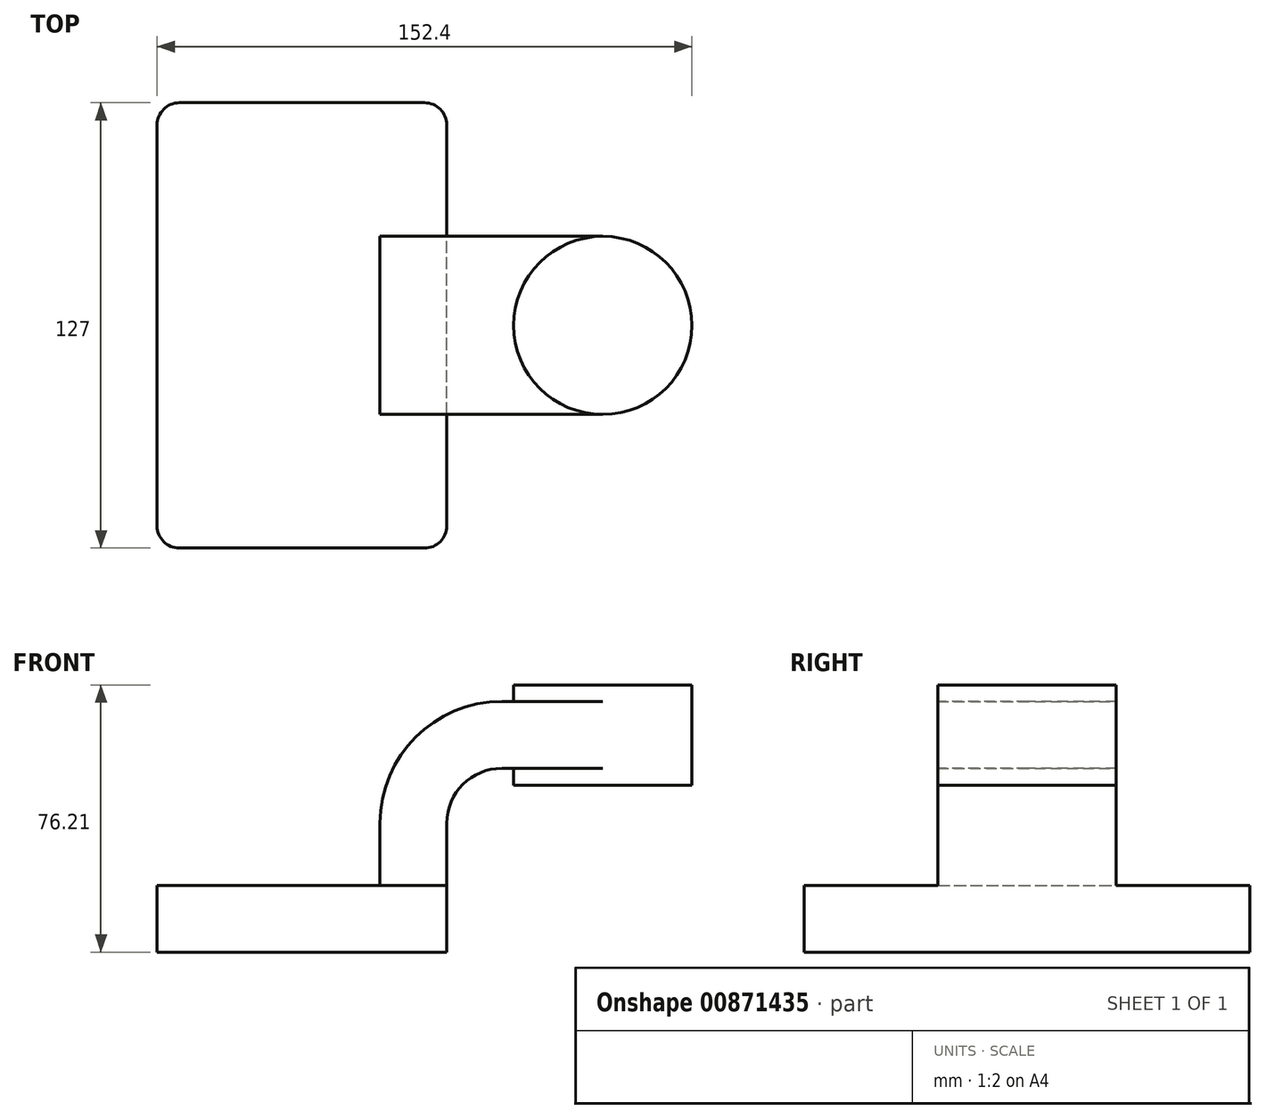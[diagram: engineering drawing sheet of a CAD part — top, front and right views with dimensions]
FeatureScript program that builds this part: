
annotation { "Feature Type Name" : "Feature", "Feature Type Description" : "" }
export const myFeature = defineFeature(function(context is Context, id is Id, definition is map)
    precondition{}
    {
        {
            var Q0;
            Q0=qCreatedBy(makeId("Front.planeOp"),FACE);
            var sketch = newSketch(context, id + "F0", { "sketchPlane" : qUnion([Q0])});
            skLineSegment(sketch, "E0.bottom", {"start": v(-41.27, -9.53) * mm, "end": v(41.28, -9.53) * mm});
            skLineSegment(sketch, "E0.top", {"start": v(-41.28, 9.53) * mm, "end": v(41.27, 9.53) * mm});
            skLineSegment(sketch, "E0.left", {"start": v(-41.27, -9.53) * mm, "end": v(-41.28, 9.53) * mm});
            skLineSegment(sketch, "E0.right", {"start": v(41.28, -9.53) * mm, "end": v(41.27, 9.53) * mm});
            skPoint(sketch, "E0.middle", {"position": v(0, 0) * mm});
            skLineSegment(sketch, "E1.bottom", {"start": v(111.12, 38.1) * mm, "end": v(60.33, 38.1) * mm});
            skLineSegment(sketch, "E1.top", {"start": v(111.13, 66.67) * mm, "end": v(60.33, 66.67) * mm});
            skLineSegment(sketch, "E1.left", {"start": v(111.12, 38.1) * mm, "end": v(111.12, 66.68) * mm});
            skLineSegment(sketch, "E1.right", {"start": v(60.33, 38.1) * mm, "end": v(60.33, 66.67) * mm});
            skPoint(sketch, "E1.middle", {"position": v(85.73, 52.39) * mm});
            skLineSegment(sketch, "E2", {"start": v(41.27, 9.53) * mm, "end": v(41.27, 27.2) * mm});
            skArc(sketch, "E3", {"start": v(41.27, 27.2) * mm, "mid": v(45.86, 38.29) * mm, "end": v(56.94, 42.88) * mm});
            skLineSegment(sketch, "E4", {"start": v(56.94, 42.88) * mm, "end": v(85.73, 42.88) * mm});
            skLineSegment(sketch, "E5.0", {"start": v(56.94, 61.93) * mm, "end": v(85.73, 61.93) * mm});
            skArc(sketch, "E5.1", {"start": v(22.22, 27.2) * mm, "mid": v(32.4, 51.76) * mm, "end": v(56.94, 61.93) * mm});
            skLineSegment(sketch, "E5.2", {"start": v(22.22, 9.53) * mm, "end": v(22.22, 27.2) * mm});
            skLineSegment(sketch, "E6", {"start": v(85.72, 38.1) * mm, "end": v(85.73, 66.67) * mm});
            skFitSpline(sketch, "E7", {"points": [v(-41.28, 9.53) * mm, v(56.94, 61.93) * mm], "startDerivative": vector(36.3, 95.17) * mm, "endDerivative": vector(111.48, -4.74) * mm});
            skSolve(sketch);
        }
        {
            var Q0;
            Q0=makeQuery(id+"F0.imprint","IMPRINT",FACE,{"disambiguationData":[TD([[makeQuery(id+"F0.imprint","IMPRINT",EDGE,{"derivedFrom":sQuery(id+"F0.wireOp",EDGE,"E0.bottom")}),1.0]])]});
            extrude(context, id + "F1", {"entities" : qUnion([Q0]), "endBound" : BoundingType.SYMMETRIC, "depth" : 127 * mm, "offsetDistance" : 25.4 * mm});
        }
        {
            var Q0;
            {var subQ1=sQuery(id+"F0.wireOp",EDGE,"E2");Q0=makeQuery(id+"F0.imprint","IMPRINT",FACE,{"disambiguationData":[TD([[makeQuery(id+"F0.imprint","IMPRINT",EDGE,{"derivedFrom":subQ1}),1.0]])]});}
            var Q1;
            {var subQ0=sQuery(id+"F0.wireOp",EDGE,"E4");var subQ1=sQuery(id+"F0.wireOp",EDGE,"E1.right");var subQ2=makeQuery(id+"F0.imprint","INTERSECT",VERTEX,{"derivedFrom":[subQ1,subQ0]});Q1=makeQuery(id+"F0.imprint","IMPRINT",FACE,{"disambiguationData":[TD([[makeQuery(id+"F0.imprint","IMPRINT",EDGE,{"disambiguationData":[TD([[subQ2,-1.0]])],"derivedFrom":subQ1}),-1.0]])]});}
            extrude(context, id + "F2", {"entities" : qUnion([Q0, Q1]), "operationType" : NewBodyOperationType.ADD, "endBound" : BoundingType.SYMMETRIC, "depth" : 50.8 * mm, "offsetDistance" : 25.4 * mm});
        }
        {
            var Q0;
            Q0=makeQuery(id+"F0.imprint","IMPRINT",FACE,{"disambiguationData":[TD([[makeQuery(id+"F0.imprint","IMPRINT",EDGE,{"derivedFrom":sQuery(id+"F0.wireOp",EDGE,"E5.1")}),1.0]])]});
            extrude(context, id + "F3", {"entities" : qUnion([Q0]), "operationType" : NewBodyOperationType.ADD, "endBound" : BoundingType.SYMMETRIC, "depth" : 15.88 * mm, "offsetDistance" : 25.4 * mm});
        }
        {
            var Q0;
            {var subQ4=sQuery(id+"F0.wireOp",EDGE,"E1.left");Q0=makeQuery(id+"F0.imprint","IMPRINT",FACE,{"disambiguationData":[TD([[makeQuery(id+"F0.imprint","IMPRINT",EDGE,{"derivedFrom":subQ4}),1.0]])]});}
            var Q1;
            Q1=sQuery(id+"F0.wireOp",EDGE,"E6");
            revolve(context, id + "F4", {"operationType" : NewBodyOperationType.ADD, "surfaceOperationType" : NewSurfaceOperationType.NEW, "entities" : qUnion([Q0]), "axis" : qUnion([Q1]), "revolveType" : RevolveType.FULL});
        }
        {
            var Q0;
            Q0=makeQuery(id+"F1.opExtrude","CAP_EDGE",EDGE,{"disambiguationData":[OSD([sQuery(id+"F0.wireOp",EDGE,"E0.right")])],"isStart":false});
            var Q1;
            Q1=makeQuery(id+"F1.opExtrude","CAP_EDGE",EDGE,{"disambiguationData":[OSD([sQuery(id+"F0.wireOp",EDGE,"E0.left")])],"isStart":false});
            var Q2;
            Q2=makeQuery(id+"F1.opExtrude","CAP_EDGE",EDGE,{"disambiguationData":[OSD([sQuery(id+"F0.wireOp",EDGE,"E0.right")])],"isStart":true});
            var Q3;
            Q3=makeQuery(id+"F1.opExtrude","CAP_EDGE",EDGE,{"disambiguationData":[OSD([sQuery(id+"F0.wireOp",EDGE,"E0.left")])],"isStart":true});
            fillet(context, id + "F5", {"entities" : qUnion([Q0, Q1, Q2, Q3]), "radius" : 6.35 * mm, "tangentPropagation" : true, "allowEdgeOverflow" : false});
        }
    });
